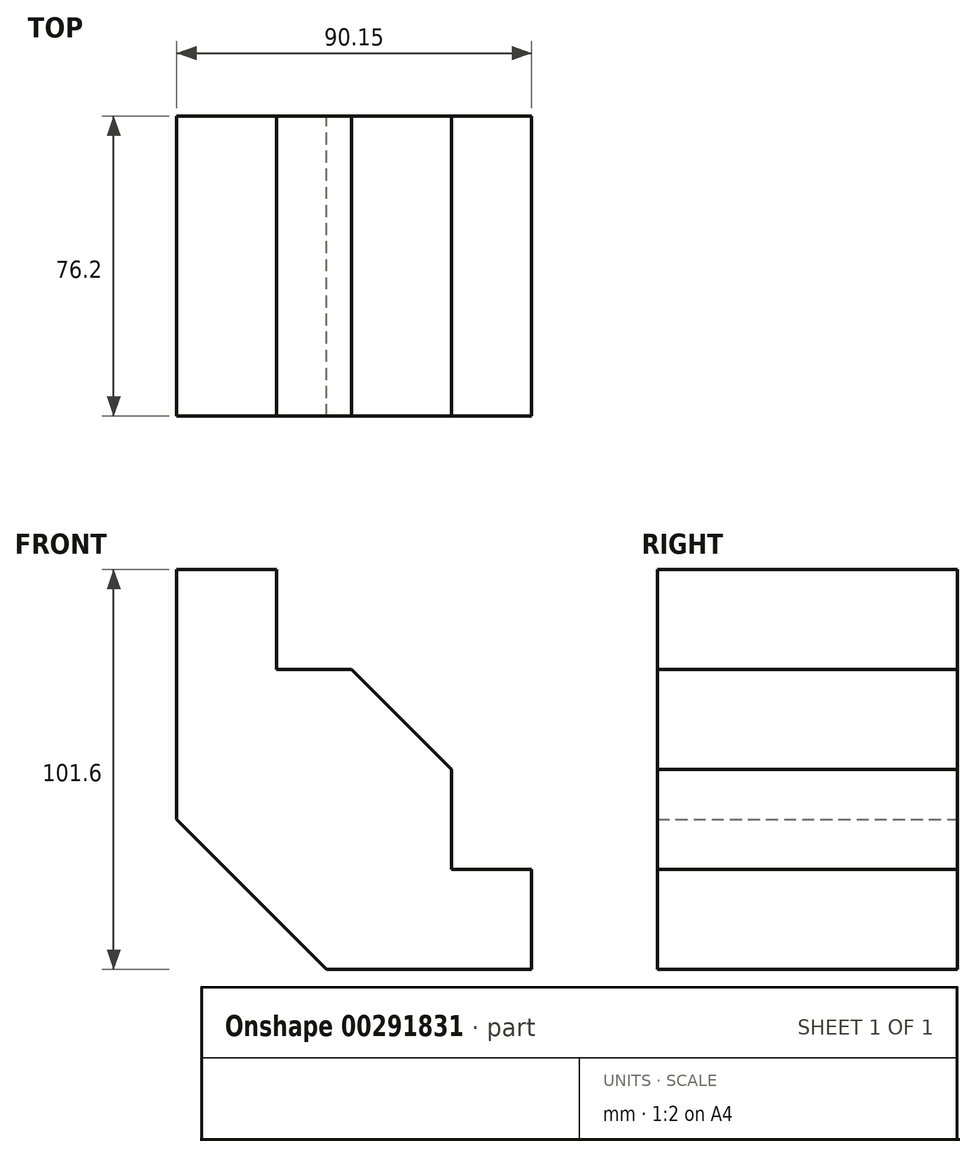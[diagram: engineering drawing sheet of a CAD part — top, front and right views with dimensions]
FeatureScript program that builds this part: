
annotation { "Feature Type Name" : "Feature", "Feature Type Description" : "" }
export const myFeature = defineFeature(function(context is Context, id is Id, definition is map)
    precondition{}
    {
        {
            var Q0;
            Q0=qCreatedBy(makeId("Front.planeOp"),FACE);
            var sketch = newSketch(context, id + "F0", { "sketchPlane" : qUnion([Q0])});
            skLineSegment(sketch, "E0", {"start": v(-90.15, 63.5) * mm, "end": v(-90.15, 0) * mm});
            skLineSegment(sketch, "E1", {"start": v(-90.15, 0) * mm, "end": v(-52.05, -38.1) * mm});
            skLineSegment(sketch, "E2", {"start": v(-52.05, -38.1) * mm, "end": v(0, -38.1) * mm});
            skLineSegment(sketch, "E3", {"start": v(0, -38.1) * mm, "end": v(0, -12.7) * mm});
            skLineSegment(sketch, "E4", {"start": v(0, -12.7) * mm, "end": v(-20.3, -12.7) * mm});
            skLineSegment(sketch, "E5", {"start": v(-20.3, -12.7) * mm, "end": v(-20.3, 12.7) * mm});
            skLineSegment(sketch, "E6", {"start": v(-20.3, 12.7) * mm, "end": v(-45.7, 38.1) * mm});
            skLineSegment(sketch, "E7", {"start": v(-45.7, 38.1) * mm, "end": v(-64.75, 38.1) * mm});
            skLineSegment(sketch, "E8", {"start": v(-64.75, 38.1) * mm, "end": v(-64.75, 63.5) * mm});
            skLineSegment(sketch, "E9", {"start": v(-64.75, 63.5) * mm, "end": v(-90.15, 63.5) * mm});
            skLineSegment(sketch, "E10", {"start": v(-52.05, -38.1) * mm, "end": v(-85.38, -38.1) * mm, "construction": true});
            skSolve(sketch);
        }
        {
            var Q0;
            Q0=makeQuery(id+"F0.imprint","IMPRINT",FACE,{"disambiguationData":[TD([[makeQuery(id+"F0.imprint","IMPRINT",EDGE,{"derivedFrom":sQuery(id+"F0.wireOp",EDGE,"E0")}),1.0]])]});
            extrude(context, id + "F1", {"entities" : qUnion([Q0]), "depth" : 76.2 * mm, "offsetDistance" : 25.4 * mm});
        }
    });
